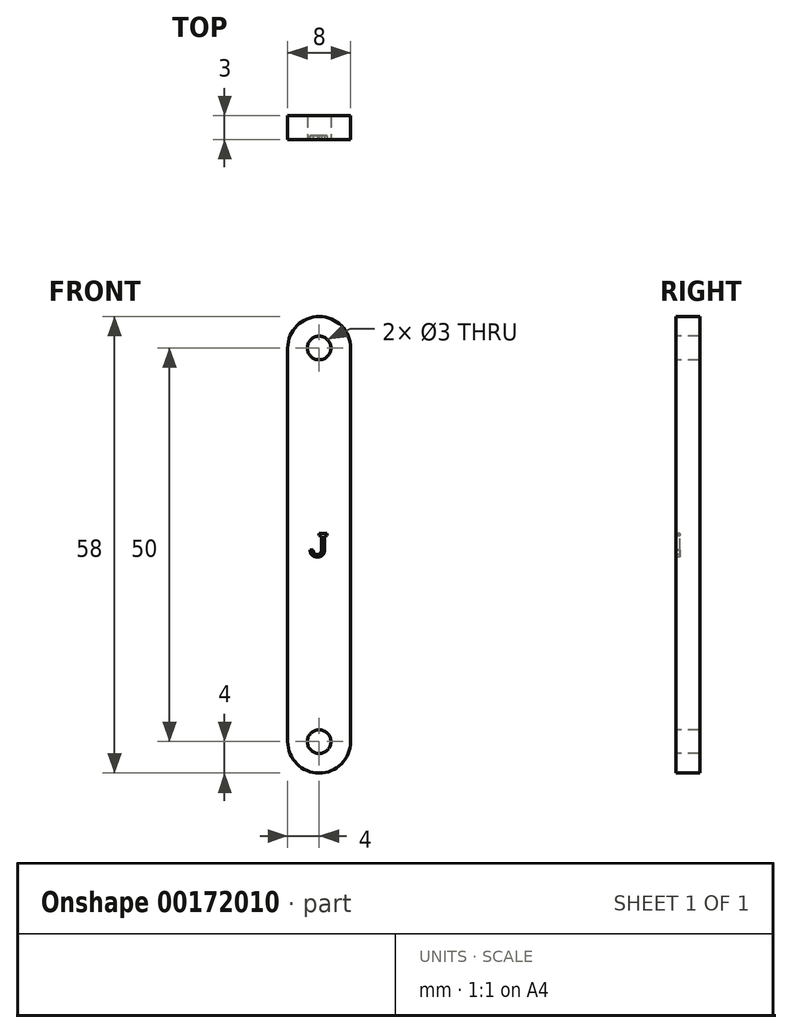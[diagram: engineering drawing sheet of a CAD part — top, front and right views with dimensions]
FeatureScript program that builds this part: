
annotation { "Feature Type Name" : "Feature", "Feature Type Description" : "" }
export const myFeature = defineFeature(function(context is Context, id is Id, definition is map)
    precondition{}
    {
        {
            assignVariable(context, id + "F0", {"name" : "Thickness", "anyValue" : 3});
        }
        {
            var Q0;
            Q0=qCreatedBy(makeId("Front.planeOp"),FACE);
            var sketch = newSketch(context, id + "F1", { "sketchPlane" : qUnion([Q0])});
            skCircle(sketch, "E0", {"center": v(0, 50) * mm, "radius": 1.5 * mm});
            skCircle(sketch, "E1", {"center": v(0, 0) * mm, "radius": 1.5 * mm});
            skArc(sketch, "E2", {"start": v(4, 50) * mm, "mid": v(0, 54) * mm, "end": v(-4, 50) * mm});
            skArc(sketch, "E3", {"start": v(-4, 0) * mm, "mid": v(0, -4) * mm, "end": v(4, 0) * mm});
            skLineSegment(sketch, "E4", {"start": v(-4, 0) * mm, "end": v(-4, 50) * mm});
            skLineSegment(sketch, "E5", {"start": v(4, 50) * mm, "end": v(4, 0) * mm});
            skSolve(sketch);
        }
        {
            var Q0;
            Q0=makeQuery(id+"F1.imprint","IMPRINT",FACE,{"disambiguationData":[TD([[makeQuery(id+"F1.imprint","IMPRINT",EDGE,{"derivedFrom":sQuery(id+"F1.wireOp",EDGE,"E0")}),-1.0]])]});
            extrude(context, id + "F2", {"entities" : qUnion([Q0]), "oppositeDirection" : true, "depth" : (getVariable(context, 'Thickness')) * mm});
        }
        {
            var Q0;
            Q0=qCreatedBy(makeId("Front.planeOp"),FACE);
            var sketch = newSketch(context, id + "F3", { "sketchPlane" : qUnion([Q0])});
            skText(sketch, "E6", { "text": "J", "fontName": "RobotoSlab-Regular.ttf"});
            skLineSegment(sketch, "E7", {"start": v(1.27, 25) * mm, "end": v(4, 25) * mm, "construction": true});
            const initialGuessF3  = {"E6": [-0.00127, 0.0235, 1, 0, 0.003]};
            skSetInitialGuess(sketch, initialGuessF3);
            skSolve(sketch);
        }
        {
            assignVariable(context, id + "F4", {"name" : "DepthText", "anyValue" : .5});
        }
        {
            var Q0;
            Q0 = qSketchRegion(id + "F3", true);
            extrude(context, id + "F5", {"entities" : qUnion([Q0]), "operationType" : NewBodyOperationType.REMOVE, "oppositeDirection" : true, "depth" : (getVariable(context, 'DepthText')) * mm});
        }
    });
